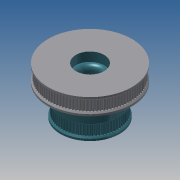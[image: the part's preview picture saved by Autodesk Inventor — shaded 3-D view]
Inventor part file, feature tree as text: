
AUTODESK INVENTOR PART (.ipt)
format: ipt  version: 2013 (Build 170138000, 138)  size: 1,229,312 bytes
history: native  units: mm
features: extrude x10, sketch x10, other x3, fillet x3, pattern_circular x1, chamfer x1
ambient origin geometry x8: Origin, YZ Plane, XZ Plane, XY Plane, X Axis, Y Axis, Z Axis, Center Point
bodies: Solid1 (feature_tree)
feature tree (28):
  other  "z idler pulley 2.iam"
  other  "100 pulley blank.ipt:1"
  other  "100 pulley blank.ipt:2"
  extrude  "Extrusion1"  Depth=10.0mm TaperAngle=0.0deg
  extrude  "Extrusion2"  Depth=10.0mm TaperAngle=0.0deg
  extrude  "Extrusion3"  Depth=7.0mm TaperAngle=0.0deg
  extrude  "Extrusion4"  Depth=7.0mm TaperAngle=0.0deg
  fillet  "Fillet1"  Radius=3.5mm
  fillet  "Fillet2"  Radius=3.5mm
  extrude  "Extrusion5"  Depth=44.055384mm
  extrude  "Extrusion6"  Depth=1.59mm
  extrude  "Extrusion7"  Depth=700.0mm TaperAngle=360.0deg
  pattern_circular  "Circular Pattern1"  Angle=45.0deg  [1 undecoded]
  extrude  "Extrusion8"  Depth=22.0mm
  extrude  "Extrusion9"  Depth=7.0mm TaperAngle=0.0deg
  chamfer  "Chamfer1"  Distance=3.5mm
  extrude  "Extrusion10"  [1 undecoded]
  fillet  "Fillet3"  [1 undecoded]
  sketch  "Sketch1"  dims[d0=10.0mm d1=10.0mm d2=0.0mm]
  sketch  "Sketch2"  dims[d3=15.0mm d5=10.0mm d6=0.0mm]
  sketch  "Sketch3"  dims[d7=22.0mm d9=7.0mm d10=0.0mm]
  sketch  "Sketch4"  dims[d11=22.0mm d13=7.0mm d14=0.0mm d15=3.5mm d16=3.5mm]
  sketch  "Sketch5"  dims[d17=23.4mm d18=0.0mm d19=44.055384mm]
  sketch  "Sketch6"  dims[d21=23.4mm d22=0.0mm d23=1.59mm]
  sketch  "Sketch7"  dims[d25=23.4mm d26=0.0mm d27=700.0mm d28=360.0deg]
  sketch  "Sketch8"  dims[d30=1.0mm]
  sketch  "Sketch9"  dims[d31=12.9mm d32=0.0mm]
  sketch  "Sketch10"  dims[d33=2.5mm d34=0.0mm d35=1.0mm d36=2.0mm d37=45.0deg d38=22.0mm d40=7.0mm d41=0.0mm d42=3.5mm]
note: 3 required parameter values undecoded (feature->parameter linkage not recoverable at this tier; creation-order binding heuristic only, values carry confidence <= 0.55)
